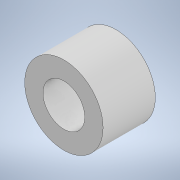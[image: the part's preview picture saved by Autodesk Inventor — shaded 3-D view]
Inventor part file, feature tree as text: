
AUTODESK INVENTOR PART (.ipt)
format: ipt  version: 2020 (Build 240168000, 168)  size: 97,792 bytes
history: native  units: in
note: dims shown in document units (in); Inventor stores cm internally (conversion verified against a paired STEP export)
features: extrude x1, sketch x1
ambient origin geometry x8: Origin, YZ Plane, XZ Plane, XY Plane, X Axis, Y Axis, Z Axis, Center Point
bodies: Solid1 (feature_tree)
feature tree (2):
  extrude  "Extrusion1"  Depth=0.1575in
  sketch  "Sketch1"  dims[d0=0.126in d1=0.2362in d2=0.1575in d3=0.0in]
